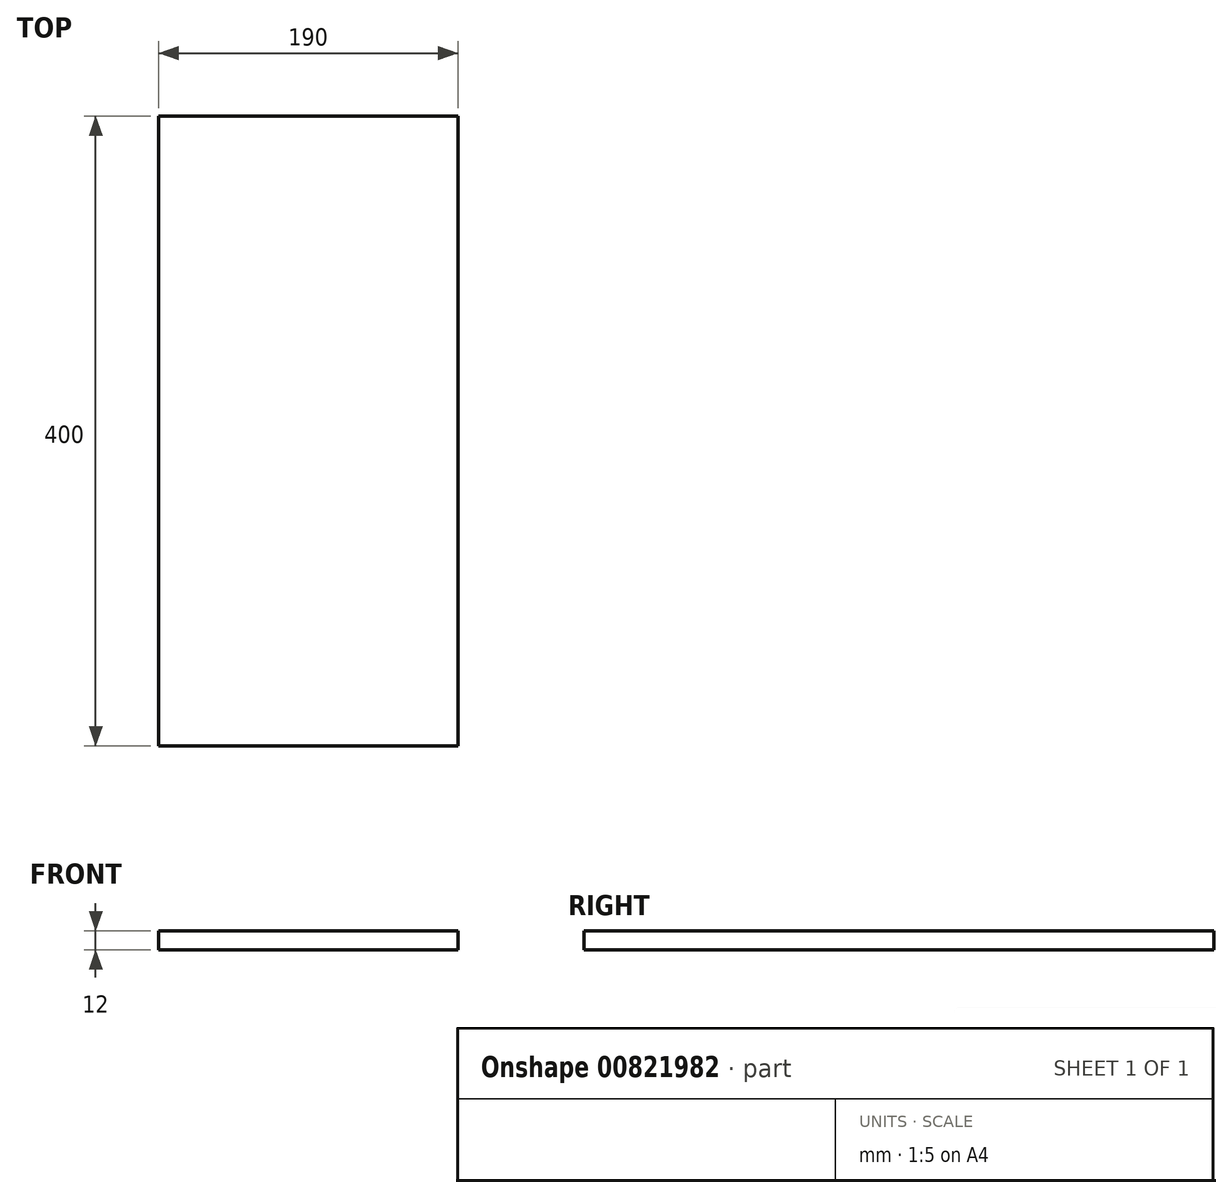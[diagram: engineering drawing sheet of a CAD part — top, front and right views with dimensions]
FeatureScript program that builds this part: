
annotation { "Feature Type Name" : "Feature", "Feature Type Description" : "" }
export const myFeature = defineFeature(function(context is Context, id is Id, definition is map)
    precondition{}
    {
        {
            var Q0;
            Q0=qCreatedBy(makeId("Top.planeOp"),FACE);
            var sketch = newSketch(context, id + "F0", { "sketchPlane" : qUnion([Q0])});
            skLineSegment(sketch, "E0.bottom", {"start": v(-133.49, 363.14) * mm, "end": v(56.51, 363.14) * mm});
            skLineSegment(sketch, "E0.top", {"start": v(-133.49, -36.86) * mm, "end": v(56.51, -36.86) * mm});
            skLineSegment(sketch, "E0.left", {"start": v(-133.49, 363.14) * mm, "end": v(-133.49, -36.86) * mm});
            skLineSegment(sketch, "E0.right", {"start": v(56.51, 363.14) * mm, "end": v(56.51, -36.86) * mm});
            skSolve(sketch);
        }
        {
            var Q0;
            Q0=makeQuery(id+"F0.imprint","IMPRINT",FACE,{"disambiguationData":[TD([[makeQuery(id+"F0.imprint","IMPRINT",EDGE,{"derivedFrom":sQuery(id+"F0.wireOp",EDGE,"E0.bottom")}),-1.0]])]});
            extrude(context, id + "F1", {"entities" : qUnion([Q0]), "depth" : 12 * mm, "offsetDistance" : 25 * mm});
        }
    });
